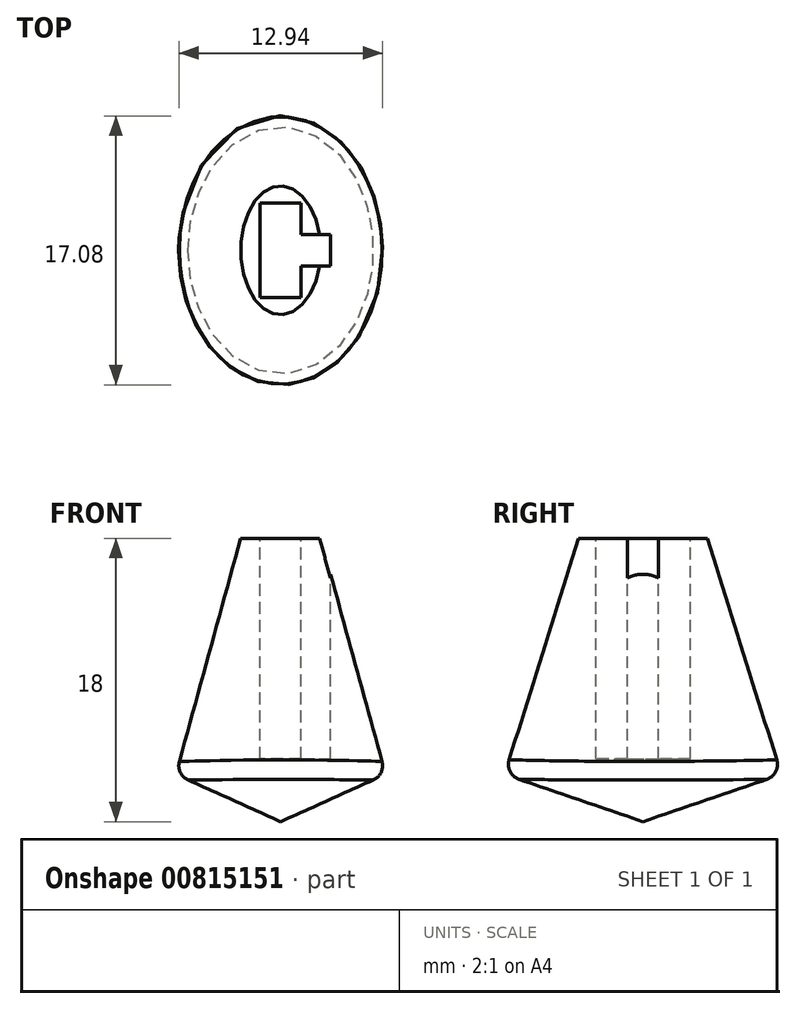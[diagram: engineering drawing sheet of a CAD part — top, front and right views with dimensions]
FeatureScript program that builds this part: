
annotation { "Feature Type Name" : "Feature", "Feature Type Description" : "" }
export const myFeature = defineFeature(function(context is Context, id is Id, definition is map)
    precondition{}
    {
        {
            var Q0;
            Q0=qCreatedBy(makeId("Top.planeOp"),FACE);
            var sketch = newSketch(context, id + "F0", { "sketchPlane" : qUnion([Q0])});
            skPoint(sketch, "E0.middle", {"position": v(0, 0) * mm});
            skEllipse(sketch, "E1", {"center": v(0, 0) * mm, "majorRadius": 8.79 * mm, "minorRadius": 6.66 * mm, "majorAxis": v(0, -1)});
            skSolve(sketch);
        }
        {
            var Q0;
            Q0=qCreatedBy(makeId("Top.planeOp"),FACE);
            cPlane(context, id + "F1", {"entities" : qUnion([Q0]), "cplaneType" : CPlaneType.OFFSET, "offset" : 15 * mm, "width" : 150 * mm, "height" : 150 * mm});
        }
        {
            var Q0;
            Q0=qCreatedBy(id+"F1.planeOp",FACE);
            var sketch = newSketch(context, id + "F2", { "sketchPlane" : qUnion([Q0])});
            skEllipse(sketch, "E2", {"center": v(0, 0) * mm, "majorRadius": 4.08 * mm, "minorRadius": 2.54 * mm, "majorAxis": v(0, -1)});
            skSolve(sketch);
        }
        {
            var Q0;
            Q0=makeQuery(id+"F0.imprint","IMPRINT",FACE,{"disambiguationData":[TD([[makeQuery(id+"F0.imprint","IMPRINT",EDGE,{"derivedFrom":sQuery(id+"F0.wireOp",EDGE,"E1")}),1.0]])]});
            var Q1;
            Q1=makeQuery(id+"F2.imprint","IMPRINT",FACE,{"disambiguationData":[TD([[makeQuery(id+"F2.imprint","IMPRINT",EDGE,{"derivedFrom":sQuery(id+"F2.wireOp",EDGE,"E2")}),1.0]])]});
            loft(context, id + "F3", {"sheetProfilesArray" : [{ "sheetProfileEntities" : qUnion([Q0]) }, { "sheetProfileEntities" : qUnion([Q1]) }]});
        }
        {
            var Q0;
            Q0=makeQuery(id+"F3.opLoft","CAP_FACE",FACE,{"disambiguationData":[OSD([makeQuery(id+"F2.imprint","IMPRINT",FACE,{"disambiguationData":[TD([[makeQuery(id+"F2.imprint","IMPRINT",EDGE,{"derivedFrom":sQuery(id+"F2.wireOp",EDGE,"E2")}),1.0]])]})])],"isStart":true});
            var sketch = newSketch(context, id + "F4", { "sketchPlane" : qUnion([Q0])});
            skLineSegment(sketch, "E3.bottom", {"start": v(1.3, -3) * mm, "end": v(-1.3, -3) * mm});
            skLineSegment(sketch, "E3.top", {"start": v(1.3, 3) * mm, "end": v(-1.3, 3) * mm});
            skLineSegment(sketch, "E3.right", {"start": v(-1.3, -3) * mm, "end": v(-1.3, 3) * mm});
            skPoint(sketch, "E3.middle", {"position": v(0, 0) * mm});
            skLineSegment(sketch, "E4.left", {"start": v(3.17, -1) * mm, "end": v(3.17, 1) * mm});
            skLineSegment(sketch, "E5", {"start": v(1.3, 3) * mm, "end": v(1.3, 1) * mm});
            skLineSegment(sketch, "E6", {"start": v(1.3, 1) * mm, "end": v(3.17, 1) * mm});
            skLineSegment(sketch, "E7", {"start": v(3.17, -1) * mm, "end": v(1.3, -1) * mm});
            skLineSegment(sketch, "E8", {"start": v(1.3, -1) * mm, "end": v(1.3, -3) * mm});
            skSolve(sketch);
        }
        {
            var Q0;
            Q0=makeQuery(id+"F4.imprint","IMPRINT",FACE,{"disambiguationData":[TD([[makeQuery(id+"F4.imprint","IMPRINT",EDGE,{"derivedFrom":sQuery(id+"F4.wireOp",EDGE,"E3.bottom")}),-1.0]])]});
            var Q1;
            {var subQ0=sQuery(id+"F4.wireOp",EDGE,"E4.left");Q1=makeQuery(id+"F4.imprint","IMPRINT",FACE,{"disambiguationData":[TD([[makeQuery(id+"F4.imprint","IMPRINT",EDGE,{"derivedFrom":subQ0}),1.0]])]});}
            extrude(context, id + "F5", {"entities" : qUnion([Q0, Q1]), "operationType" : NewBodyOperationType.REMOVE, "oppositeDirection" : true, "depth" : 14 * mm, "offsetDistance" : 25 * mm});
        }
        {
            var Q0;
            Q0=qCreatedBy(makeId("Top.planeOp"),FACE);
            cPlane(context, id + "F6", {"entities" : qUnion([Q0]), "cplaneType" : CPlaneType.OFFSET, "offset" : 3 * mm, "oppositeDirection" : true, "width" : 150 * mm, "height" : 150 * mm});
        }
        {
            var Q0;
            Q0=qCreatedBy(id+"F6.planeOp",FACE);
            var sketch = newSketch(context, id + "F7", { "sketchPlane" : qUnion([Q0])});
            skPoint(sketch, "E9", {"position": v(0, 0) * mm});
            skSolve(sketch);
        }
        {
            var Q1;
            Q1=makeQuery(id+"F3.opLoft","CAP_FACE",FACE,{"disambiguationData":[OSD([makeQuery(id+"F0.imprint","IMPRINT",FACE,{"disambiguationData":[TD([[makeQuery(id+"F0.imprint","IMPRINT",EDGE,{"derivedFrom":sQuery(id+"F0.wireOp",EDGE,"E1")}),1.0]])]})])],"isStart":true});
            var Q2;
            Q2=sQuery(id+"F7.wireOp",VERTEX,"E9");
            loft(context, id + "F8", {"operationType" : NewBodyOperationType.ADD, "sheetProfilesArray" : [{ "sheetProfileEntities" : qUnion([Q1]) }, { "sheetProfileEntities" : qUnion([Q2]) }]});
        }
        {
            var Q0;
            Q0=makeQuery(id+"F8.opLoft","SWEPT_FACE",FACE,{"disambiguationData":[OSD([sQuery(id+"F0.wireOp",EDGE,"E1"),sQuery(id+"F7.wireOp",VERTEX,"E9")])]});
            fillet(context, id + "F9", {"entities" : qUnion([Q0]), "radius" : 1 * mm, "tangentPropagation" : true, "allowEdgeOverflow" : false});
        }
    });
